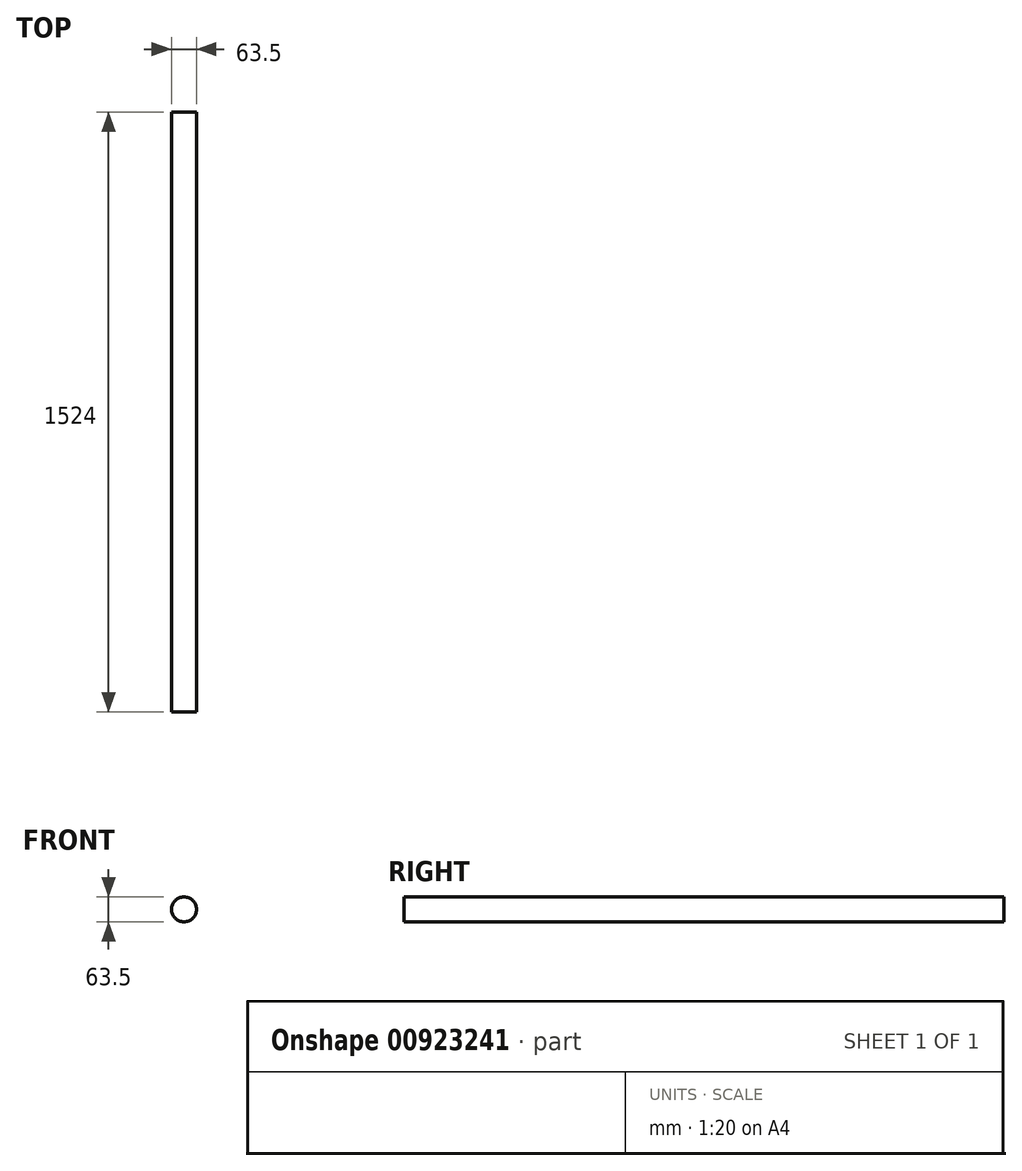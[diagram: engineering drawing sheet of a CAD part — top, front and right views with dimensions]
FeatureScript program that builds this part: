
annotation { "Feature Type Name" : "Feature", "Feature Type Description" : "" }
export const myFeature = defineFeature(function(context is Context, id is Id, definition is map)
    precondition{}
    {
        {
            var Q0;
            Q0=qCreatedBy(makeId("Front.planeOp"),FACE);
            var sketch = newSketch(context, id + "F0", { "sketchPlane" : qUnion([Q0])});
            skCircle(sketch, "E0", {"center": v(0, 0) * mm, "radius": 31.75 * mm});
            skSolve(sketch);
        }
        {
            var Q0;
            Q0=makeQuery(id+"F0.imprint","IMPRINT",FACE,{"disambiguationData":[TD([[makeQuery(id+"F0.imprint","IMPRINT",EDGE,{"derivedFrom":sQuery(id+"F0.wireOp",EDGE,"E0")}),1.0]])]});
            extrude(context, id + "F1", {"entities" : qUnion([Q0]), "depth" : 1524 * mm, "offsetDistance" : 25.4 * mm, "symmetric" : true});
        }
    });
